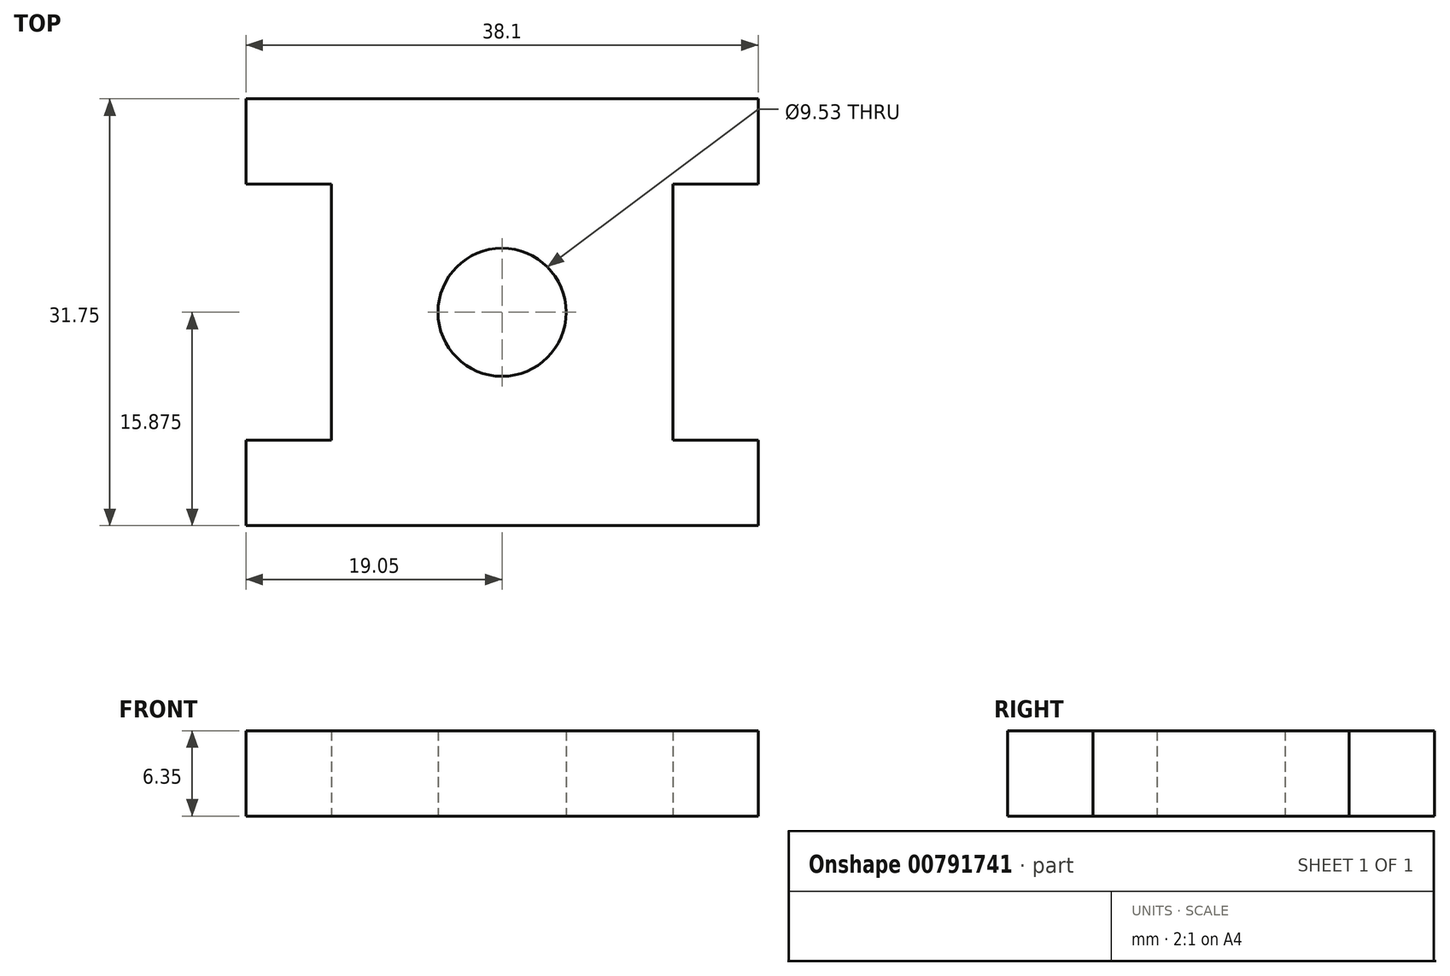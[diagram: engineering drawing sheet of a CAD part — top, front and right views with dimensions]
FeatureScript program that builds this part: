
annotation { "Feature Type Name" : "Feature", "Feature Type Description" : "" }
export const myFeature = defineFeature(function(context is Context, id is Id, definition is map)
    precondition{}
    {
        {
            var Q0;
            Q0=qCreatedBy(makeId("Top.planeOp"),FACE);
            var sketch = newSketch(context, id + "F0", { "sketchPlane" : qUnion([Q0])});
            skLineSegment(sketch, "E0.bottom", {"start": v(0, 0) * mm, "end": v(38.1, 0) * mm});
            skLineSegment(sketch, "E0.top", {"start": v(0, 31.75) * mm, "end": v(38.1, 31.75) * mm});
            skLineSegment(sketch, "E0.left", {"start": v(0, 0) * mm, "end": v(0, 6.35) * mm});
            skLineSegment(sketch, "E0.right", {"start": v(38.1, 0) * mm, "end": v(38.1, 6.35) * mm});
            skLineSegment(sketch, "E1.bottom", {"start": v(0, 6.35) * mm, "end": v(6.35, 6.35) * mm});
            skLineSegment(sketch, "E1.top", {"start": v(0, 25.4) * mm, "end": v(6.35, 25.4) * mm});
            skLineSegment(sketch, "E1.right", {"start": v(6.35, 6.35) * mm, "end": v(6.35, 25.4) * mm});
            skLineSegment(sketch, "E2.bottom", {"start": v(38.1, 6.35) * mm, "end": v(31.75, 6.35) * mm});
            skLineSegment(sketch, "E2.top", {"start": v(38.1, 25.4) * mm, "end": v(31.75, 25.4) * mm});
            skLineSegment(sketch, "E2.right", {"start": v(31.75, 6.35) * mm, "end": v(31.75, 25.4) * mm});
            skLineSegment(sketch, "E3.trimOffspring", {"start": v(0, 25.4) * mm, "end": v(0, 31.75) * mm});
            skLineSegment(sketch, "E4.trimOffspring", {"start": v(38.1, 25.4) * mm, "end": v(38.1, 31.75) * mm});
            skCircle(sketch, "E5", {"center": v(19.05, 15.88) * mm, "radius": 4.76 * mm});
            skSolve(sketch);
        }
        {
            var Q0;
            Q0=qSketchRegion(id+"F0",true);
            extrude(context, id + "F1", {"entities" : qUnion([Q0]), "depth" : 6.35 * mm, "offsetDistance" : 25.4 * mm});
        }
    });
